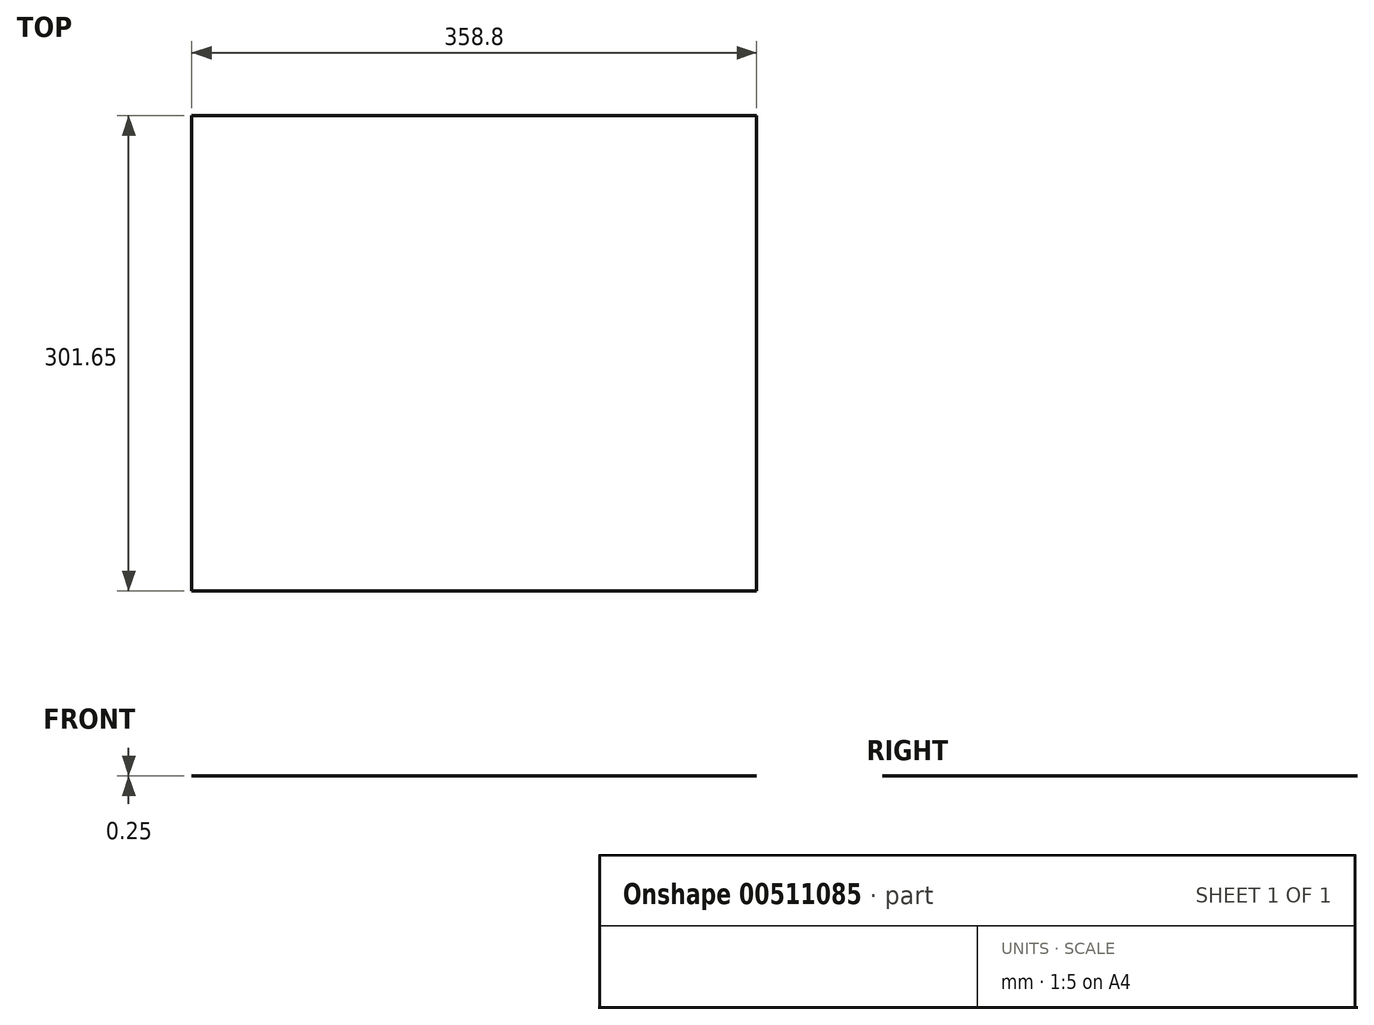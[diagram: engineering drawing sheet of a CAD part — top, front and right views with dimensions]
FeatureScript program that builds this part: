
annotation { "Feature Type Name" : "Feature", "Feature Type Description" : "" }
export const myFeature = defineFeature(function(context is Context, id is Id, definition is map)
    precondition{}
    {
        {
            assignVariable(context, id + "F0", {"name" : "plywoodThickness", "anyValue" : 0.25});
        }
        {
            var Q0;
            Q0=qCreatedBy(makeId("Top.planeOp"),FACE);
            var sketch = newSketch(context, id + "F1", { "sketchPlane" : qUnion([Q0])});
            skLineSegment(sketch, "E0.bottom", {"start": v(0, -301.65) * mm, "end": v(358.8, -301.65) * mm});
            skLineSegment(sketch, "E0.top", {"start": v(0, 0) * mm, "end": v(358.8, 0) * mm});
            skLineSegment(sketch, "E0.left", {"start": v(0, -301.65) * mm, "end": v(0, 0) * mm});
            skLineSegment(sketch, "E0.right", {"start": v(358.8, -301.65) * mm, "end": v(358.8, 0) * mm});
            skSolve(sketch);
        }
        {
            var Q0;
            Q0=makeQuery(id+"F1.imprint","IMPRINT",FACE,{"disambiguationData":[TD([[makeQuery(id+"F1.imprint","IMPRINT",EDGE,{"derivedFrom":sQuery(id+"F1.wireOp",EDGE,"E0.bottom")}),1.0]])]});
            extrude(context, id + "F2", {"entities" : qUnion([Q0]), "depth" : (getVariable(context, 'plywoodThickness')) * mm, "offsetDistance" : 25.4 * mm});
        }
    });
